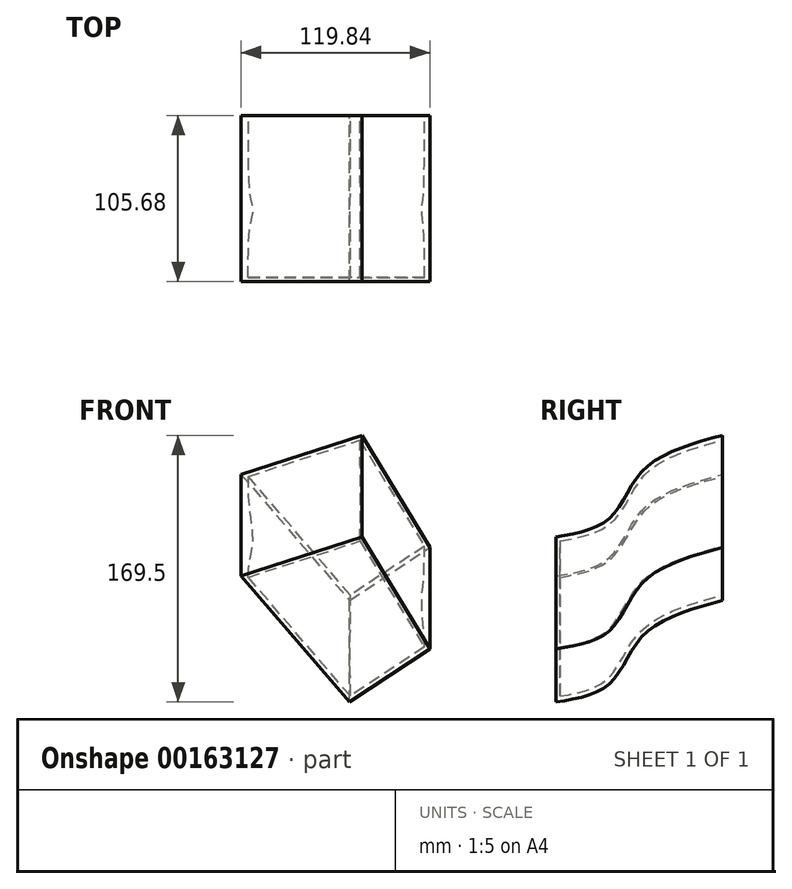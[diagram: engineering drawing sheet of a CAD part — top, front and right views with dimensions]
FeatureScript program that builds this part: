
annotation { "Feature Type Name" : "Feature", "Feature Type Description" : "" }
export const myFeature = defineFeature(function(context is Context, id is Id, definition is map)
    precondition{}
    {
        {
            var Q0;
            Q0=qCreatedBy(makeId("Front.planeOp"),FACE);
            var sketch = newSketch(context, id + "F0", { "sketchPlane" : qUnion([Q0])});
            skLineSegment(sketch, "E0", {"start": v(-57.8, 22.76) * mm, "end": v(11.1, -57.4) * mm});
            skLineSegment(sketch, "E1", {"start": v(11.1, -57.4) * mm, "end": v(62.04, -23.66) * mm});
            skLineSegment(sketch, "E2", {"start": v(62.04, -23.66) * mm, "end": v(18.82, 47.62) * mm});
            skLineSegment(sketch, "E3", {"start": v(18.82, 47.62) * mm, "end": v(-57.8, 22.76) * mm});
            skSolve(sketch);
        }
        {
            var Q0;
            Q0=qCreatedBy(makeId("Right.planeOp"),FACE);
            var sketch = newSketch(context, id + "F1", { "sketchPlane" : qUnion([Q0])});
            skFitSpline(sketch, "E4", {"points": [v(0, 0) * mm, v(34.3, 11.9) * mm, v(55.6, 42.45) * mm, v(105.68, 64.48) * mm], "startDerivative": vector(126.32, 20.59) * mm, "endDerivative": vector(153.97, 42.34) * mm});
            skSolve(sketch);
        }
        {
            var Q0;
            Q0=makeQuery(id+"F0.imprint","IMPRINT",FACE,{"disambiguationData":[TD([[makeQuery(id+"F0.imprint","IMPRINT",EDGE,{"derivedFrom":sQuery(id+"F0.wireOp",EDGE,"E0")}),1.0]])]});
            var Q1;
            Q1=sQuery(id+"F1.wireOp",EDGE,"E4");
            sweep(context, id + "F2", {"profiles" : qUnion([Q0]), "path" : qUnion([Q1]), "keepProfileOrientation" : true});
        }
        {
            var Q0;
            Q0=makeQuery(id+"F2.opSweep","CAP_FACE",FACE,{"disambiguationData":[OSD([sQuery(id+"F0.wireOp",EDGE,"E0"),sQuery(id+"F0.wireOp",EDGE,"E1"),sQuery(id+"F0.wireOp",EDGE,"E2"),sQuery(id+"F0.wireOp",EDGE,"E3"),sQuery(id+"F1.wireOp",VERTEX,"E4.end")])],"isStart":false});
            shell(context, id + "F3", {"entities" : qUnion([Q0]), "thickness" : 2.54 * mm});
        }
    });
